# Revit family: CAME_КомплектКрепления_ГоризонтальныхПланок_SALOON40_ДляОграждений
name_source: partatom
category: Специальное оборудование
units: mm (PartAtom-declared; Revit-internal decimal feet)

## family parameters
Всегда вертикально = Да
На основе рабочей плоскости = Нет
Общий = Да
При загрузке вырезать с полостями = Нет
Размер круглого соединителя = Использовать диаметр
Тип детали = Нормальный
Точка расчета площади = Нет

## types (2) — shared parameters
ADSK_URL документации изделия = https://camerussia.com
ADSK_URL страницы изделия = https://camerussia.com
ADSK_Версия Revit = 2019
ADSK_Версия семейства = 1.0
ADSK_Группирование = SALOON
ADSK_Единица измерения = шт.
ADSK_Завод-изготовитель = CAME
ADSK_Код изделия = Код КСР 26.30.50.119.61.2.07.09
ADSK_Количество = 2
ADSK_Обозначение = ТУ 26.30.50-001-89603926-2021
ADSK_Размер_Диаметр = 120 мм
BL_BIM library = https://bimlib.pro
URL = https://camerussia.com
Изготовитель = CAME
Расстояние между креплениями = 500 мм

## per-type parameters (varying)
| type | ADSK_Марка | ADSK_Масса | ADSK_Масса_Текст | ADSK_Материал | ADSK_Наименование | ADSK_Наименование краткое | Группа модели | Описание |
| Хром | АРТ:001PSSA03 | 0.11 | 0.11 | CAME_Хром | Комплект крепления горизонтальных планок ограждений для SALOON 40, хром | Крепления гор. планок SALOON 40, хром | Турникеты | Набор из двух хромированных муфтовых соединений с винтами для крепления горизонтальных планок ограждений 40 мм. |
| Нержавеющая сталь | АРТ:001PSSA04 | 0.59 | 0.59 | CAME_Сталь_Нержавеющая_AISI 304 | Комплект крепления горизонтальных планок ограждений для SALOON 40, нержавеющая сталь | Крепления гор. планок SALOON 40, нерж. сталь |  | Набор из двух муфтовых соединений из нержавеющей стали AISI 304 с винтами для крепления горизонтальных планок ограждений 40 мм. |
